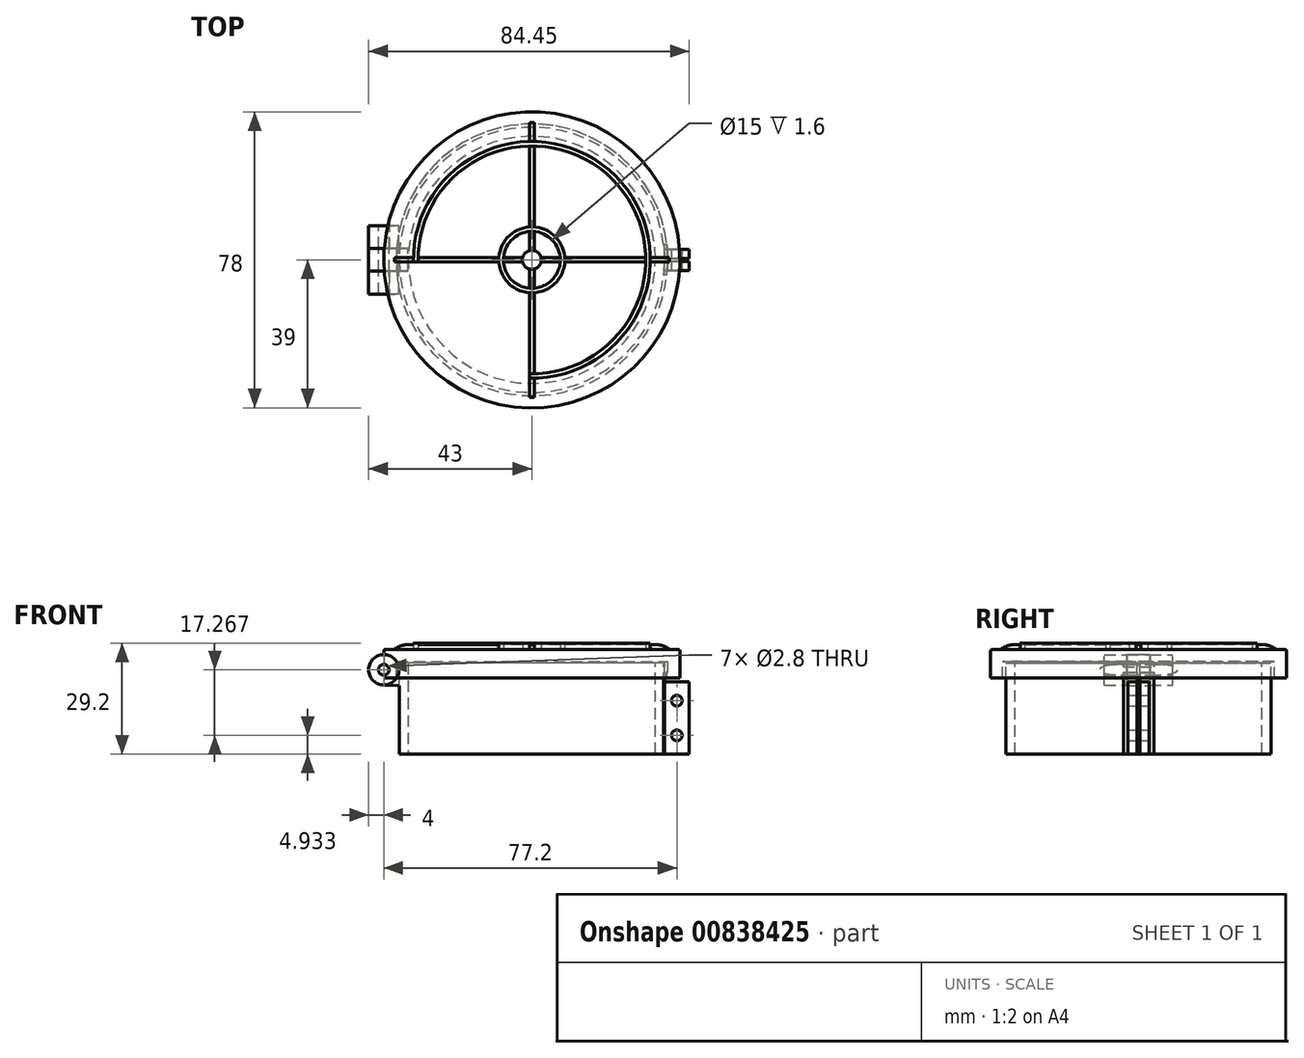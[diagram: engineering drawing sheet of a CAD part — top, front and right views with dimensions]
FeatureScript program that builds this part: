
annotation { "Feature Type Name" : "Feature", "Feature Type Description" : "" }
export const myFeature = defineFeature(function(context is Context, id is Id, definition is map)
    precondition{}
    {
        {
            var Q0;
            Q0=qCreatedBy(makeId("Front.planeOp"),FACE);
            var sketch = newSketch(context, id + "F0", { "sketchPlane" : qUnion([Q0])});
            skLineSegment(sketch, "E0", {"start": v(-39, 2) * mm, "end": v(-39, 9.6) * mm});
            skLineSegment(sketch, "E1", {"start": v(-39, 9.6) * mm, "end": v(0, 9.6) * mm});
            skLineSegment(sketch, "E2", {"start": v(0, 9.6) * mm, "end": v(0, 6.4) * mm});
            skLineSegment(sketch, "E3", {"start": v(0, 6.4) * mm, "end": v(-35.8, 6.4) * mm});
            skLineSegment(sketch, "E4", {"start": v(-35.8, 6.4) * mm, "end": v(-35.8, 2) * mm});
            skLineSegment(sketch, "E5", {"start": v(-35.8, 2) * mm, "end": v(-39, 2) * mm});
            skCircle(sketch, "E6", {"center": v(-39, 4.2) * mm, "radius": 4 * mm});
            skCircle(sketch, "E7", {"center": v(-39, 4.2) * mm, "radius": 1.4 * mm});
            skLineSegment(sketch, "E8.MirrorCS", {"start": v(39, 9.6) * mm, "end": v(0, 9.6) * mm});
            skLineSegment(sketch, "E9.MirrorCS", {"start": v(0, 6.4) * mm, "end": v(35.8, 6.4) * mm});
            skLineSegment(sketch, "E10.MirrorCS", {"start": v(35.8, 6.4) * mm, "end": v(35.8, 2) * mm});
            skLineSegment(sketch, "E11.MirrorCS", {"start": v(35.8, 2) * mm, "end": v(39, 2) * mm});
            skLineSegment(sketch, "E12.MirrorCS", {"start": v(39, 2) * mm, "end": v(39, 9.6) * mm});
            skCircle(sketch, "E13", {"center": v(35.8, 2.8) * mm, "radius": 0.8 * mm});
            skSolve(sketch);
        }
        {
            var Q0;
            Q0=qCreatedBy(makeId("Front.planeOp"),FACE);
            var sketch = newSketch(context, id + "F1", { "sketchPlane" : qUnion([Q0])});
            skLineSegment(sketch, "E14.bottom", {"start": v(-34.95, 6) * mm, "end": v(-32.55, 6) * mm});
            skLineSegment(sketch, "E14.top", {"start": v(-34.95, -18) * mm, "end": v(-32.55, -18) * mm});
            skLineSegment(sketch, "E14.left", {"start": v(-34.95, 6) * mm, "end": v(-34.95, -18) * mm});
            skLineSegment(sketch, "E14.right", {"start": v(-32.55, 6) * mm, "end": v(-32.55, -18) * mm});
            skCircle(sketch, "E15", {"center": v(-39, 4.2) * mm, "radius": 4 * mm});
            skCircle(sketch, "E16", {"center": v(-39, 4.2) * mm, "radius": 1.4 * mm});
            skLineSegment(sketch, "E17", {"start": v(-34.95, 0) * mm, "end": v(-39.2, 0.2) * mm});
            skLineSegment(sketch, "E18.MirrorCS", {"start": v(32.55, 6) * mm, "end": v(32.55, -18) * mm});
            skLineSegment(sketch, "E19.MirrorCS", {"start": v(34.95, 6) * mm, "end": v(34.95, -18) * mm});
            skLineSegment(sketch, "E20.MirrorCS", {"start": v(34.95, 6) * mm, "end": v(32.55, 6) * mm});
            skLineSegment(sketch, "E21.MirrorCS", {"start": v(34.95, -18) * mm, "end": v(32.55, -18) * mm});
            skCircle(sketch, "E22", {"center": v(34.95, 4.2) * mm, "radius": 0.8 * mm});
            skLineSegment(sketch, "E23", {"start": v(34.95, 1) * mm, "end": v(41.45, 1) * mm});
            skLineSegment(sketch, "E24", {"start": v(41.45, 1) * mm, "end": v(41.45, -18) * mm});
            skLineSegment(sketch, "E25", {"start": v(41.45, -18) * mm, "end": v(34.95, -18) * mm});
            skLineSegment(sketch, "E26", {"start": v(38.2, 1) * mm, "end": v(38.2, -18) * mm, "construction": true});
            skCircle(sketch, "E27", {"center": v(38.2, -3.93) * mm, "radius": 1.4 * mm});
            skCircle(sketch, "E28", {"center": v(38.2, -13.07) * mm, "radius": 1.4 * mm});
            skLineSegment(sketch, "E29", {"start": v(-34.95, 6) * mm, "end": v(-35.43, 6) * mm});
            skSolve(sketch);
        }
        {
            var Q0;
            {var subQ3=sQuery(id+"F1.wireOp",EDGE,"E14.bottom");Q0=makeQuery(id+"F1.imprint","IMPRINT",FACE,{"disambiguationData":[TD([[makeQuery(id+"F1.imprint","IMPRINT",EDGE,{"derivedFrom":subQ3}),-1.0]])]});}
            var Q1;
            Q1=sQuery(id+"F0.wireOp",EDGE,"E2");
            revolve(context, id + "F2", {"surfaceOperationType" : NewSurfaceOperationType.NEW, "entities" : qUnion([Q0]), "axis" : qUnion([Q1]), "revolveType" : RevolveType.FULL});
        }
        {
            var Q0;
            {var subQ0=sQuery(id+"F1.wireOp",EDGE,"E22");var subQ1=sQuery(id+"F1.wireOp",EDGE,"E19.MirrorCS");var subQ2=makeQuery(id+"F1.imprint","INTERSECT",VERTEX,{"disambiguationData":[OD(0.0)],"derivedFrom":[subQ1,subQ0]});Q0=makeQuery(id+"F1.imprint","IMPRINT",FACE,{"disambiguationData":[TD([[makeQuery(id+"F1.imprint","IMPRINT",EDGE,{"disambiguationData":[TD([[subQ2,-1.0]])],"derivedFrom":subQ1}),1.0]])]});}
            var Q1;
            {var subQ0=sQuery(id+"F1.wireOp",EDGE,"E22");var subQ1=sQuery(id+"F1.wireOp",EDGE,"E19.MirrorCS");var subQ2=makeQuery(id+"F1.imprint","INTERSECT",VERTEX,{"disambiguationData":[OD(0.0)],"derivedFrom":[subQ1,subQ0]});Q1=makeQuery(id+"F1.imprint","IMPRINT",FACE,{"disambiguationData":[TD([[makeQuery(id+"F1.imprint","IMPRINT",EDGE,{"disambiguationData":[TD([[subQ2,-1.0]])],"derivedFrom":subQ1}),-1.0]])]});}
            extrude(context, id + "F3", {"entities" : qUnion([Q0, Q1]), "operationType" : NewBodyOperationType.ADD, "endBound" : BoundingType.SYMMETRIC, "depth" : 8 * mm, "offsetDistance" : 25 * mm});
        }
        {
            var Q0;
            {var subQ1=sQuery(id+"F1.wireOp",EDGE,"E23");Q0=makeQuery(id+"F1.imprint","IMPRINT",FACE,{"disambiguationData":[TD([[makeQuery(id+"F1.imprint","IMPRINT",EDGE,{"derivedFrom":subQ1}),-1.0]])]});}
            var Q1;
            Q1=makeQuery(id+"F1.imprint","IMPRINT",FACE,{"disambiguationData":[TD([[makeQuery(id+"F1.imprint","IMPRINT",EDGE,{"derivedFrom":sQuery(id+"F1.wireOp",EDGE,"E18.MirrorCS")}),1.0]])]});
            extrude(context, id + "F4", {"entities" : qUnion([Q0, Q1]), "operationType" : NewBodyOperationType.ADD, "endBound" : BoundingType.SYMMETRIC, "depth" : 2.8 * 2 * mm, "offsetDistance" : 25 * mm});
        }
        {
            var Q0;
            Q0=qCreatedBy(makeId("Front.planeOp"),FACE);
            var sketch = newSketch(context, id + "F5", { "sketchPlane" : qUnion([Q0])});
            skLineSegment(sketch, "E30.bottom", {"start": v(30.27, 7.43) * mm, "end": v(42.44, 7.43) * mm});
            skLineSegment(sketch, "E30.top", {"start": v(30.27, -18.9) * mm, "end": v(42.44, -18.9) * mm});
            skLineSegment(sketch, "E30.left", {"start": v(30.27, 7.43) * mm, "end": v(30.27, -18.9) * mm});
            skLineSegment(sketch, "E30.right", {"start": v(42.44, 7.43) * mm, "end": v(42.44, -18.9) * mm});
            skSolve(sketch);
        }
        {
            var Q0;
            Q0=makeQuery(id+"F5.imprint","IMPRINT",FACE,{"disambiguationData":[TD([[makeQuery(id+"F5.imprint","IMPRINT",EDGE,{"derivedFrom":sQuery(id+"F5.wireOp",EDGE,"E30.bottom")}),-1.0]])]});
            extrude(context, id + "F6", {"entities" : qUnion([Q0]), "operationType" : NewBodyOperationType.REMOVE, "endBound" : BoundingType.SYMMETRIC, "depth" : 0.8 * mm, "offsetDistance" : 25 * mm});
        }
        {
            var Q0;
            Q0=makeQuery(id+"F1.imprint","IMPRINT",FACE,{"disambiguationData":[TD([[makeQuery(id+"F1.imprint","IMPRINT",EDGE,{"derivedFrom":sQuery(id+"F1.wireOp",EDGE,"E15")}),1.0]])]});
            var Q1;
            {var subQ2=sQuery(id+"F1.wireOp",EDGE,"E17");Q1=makeQuery(id+"F1.imprint","IMPRINT",FACE,{"disambiguationData":[TD([[makeQuery(id+"F1.imprint","IMPRINT",EDGE,{"derivedFrom":subQ2}),-1.0]])]});}
            var Q2;
            {var subQ3=sQuery(id+"F1.wireOp",EDGE,"E14.bottom");Q2=makeQuery(id+"F1.imprint","IMPRINT",FACE,{"disambiguationData":[TD([[makeQuery(id+"F1.imprint","IMPRINT",EDGE,{"derivedFrom":subQ3}),-1.0]])]});}
            extrude(context, id + "F7", {"entities" : qUnion([Q0, Q1, Q2]), "endBound" : BoundingType.SYMMETRIC, "depth" : 18 / 3 * mm, "offsetDistance" : 25 * mm});
        }
        {
            var Q0;
            {var subQ4=sQuery(id+"F0.wireOp",EDGE,"E1");Q0=makeQuery(id+"F0.imprint","IMPRINT",FACE,{"disambiguationData":[TD([[makeQuery(id+"F0.imprint","IMPRINT",EDGE,{"derivedFrom":subQ4}),-1.0]])]});}
            var Q1;
            {var subQ0=sQuery(id+"F0.wireOp",EDGE,"E4");Q1=makeQuery(id+"F0.imprint","IMPRINT",FACE,{"disambiguationData":[TD([[makeQuery(id+"F0.imprint","IMPRINT",EDGE,{"derivedFrom":subQ0}),-1.0]])]});}
            var Q2;
            {var subQ0=sQuery(id+"F0.wireOp",EDGE,"E7");var subQ1=sQuery(id+"F0.wireOp",EDGE,"E0");var subQ2=makeQuery(id+"F0.imprint","INTERSECT",VERTEX,{"disambiguationData":[OD(0.0)],"derivedFrom":[subQ1,subQ0]});Q2=makeQuery(id+"F0.imprint","IMPRINT",FACE,{"disambiguationData":[TD([[makeQuery(id+"F0.imprint","IMPRINT",EDGE,{"disambiguationData":[TD([[subQ2,-1.0]])],"derivedFrom":subQ1}),-1.0]])]});}
            var Q3;
            Q3=sQuery(id+"F0.wireOp",EDGE,"E2");
            revolve(context, id + "F8", {"surfaceOperationType" : NewSurfaceOperationType.NEW, "entities" : qUnion([Q0, Q1, Q2]), "axis" : qUnion([Q3]), "revolveType" : RevolveType.FULL});
        }
        {
            var Q0;
            {var subQ0=sQuery(id+"F0.wireOp",EDGE,"E4");Q0=makeQuery(id+"F0.imprint","IMPRINT",FACE,{"disambiguationData":[TD([[makeQuery(id+"F0.imprint","IMPRINT",EDGE,{"derivedFrom":subQ0}),1.0]])]});}
            var Q1;
            {var subQ0=sQuery(id+"F0.wireOp",EDGE,"E4");Q1=makeQuery(id+"F0.imprint","IMPRINT",FACE,{"disambiguationData":[TD([[makeQuery(id+"F0.imprint","IMPRINT",EDGE,{"derivedFrom":subQ0}),-1.0]])]});}
            var Q2;
            Q2=sQuery(id+"F0.wireOp",EDGE,"E6");
            var Q3;
            Q3=sQuery(id+"F0.wireOp",EDGE,"E7");
            extrude(context, id + "F9", {"entities" : qUnion([Q0, Q1]), "surfaceEntities" : qUnion([Q2, Q3]), "endBound" : BoundingType.SYMMETRIC, "depth" : 18 * mm, "offsetDistance" : 25 * mm});
        }
        {
            var Q0;
            {var subQ0=sQuery(id+"F0.wireOp",EDGE,"E4");Q0=makeQuery(id+"F0.imprint","IMPRINT",FACE,{"disambiguationData":[TD([[makeQuery(id+"F0.imprint","IMPRINT",EDGE,{"derivedFrom":subQ0}),1.0]])]});}
            var Q1;
            {var subQ0=sQuery(id+"F0.wireOp",EDGE,"E4");Q1=makeQuery(id+"F0.imprint","IMPRINT",FACE,{"disambiguationData":[TD([[makeQuery(id+"F0.imprint","IMPRINT",EDGE,{"derivedFrom":subQ0}),-1.0]])]});}
            extrude(context, id + "F10", {"entities" : qUnion([Q0, Q1]), "endBound" : BoundingType.SYMMETRIC, "oppositeDirection" : true, "depth" : 6 * mm, "offsetDistance" : 25 * mm});
        }
        {
            var Q0;
            Q0=makeQuery(id+"F10.opExtrude","SWEPT_BODY",BODY,{"disambiguationData":[OSD([sQuery(id+"F0.wireOp",EDGE,"E6"),sQuery(id+"F0.wireOp",EDGE,"E7")])]});
            var Q1;
            Q1=makeQuery(id+"F9.opExtrude","SWEPT_BODY",BODY,{"disambiguationData":[OSD([sQuery(id+"F0.wireOp",EDGE,"E6"),sQuery(id+"F0.wireOp",EDGE,"E7")])]});
            var Q2;
            Q2=makeQuery(id+"F8.opRevolve","SWEPT_BODY",BODY,{"disambiguationData":[OSD([sQuery(id+"F0.wireOp",EDGE,"E0"),sQuery(id+"F0.wireOp",EDGE,"E1"),sQuery(id+"F0.wireOp",EDGE,"E2"),sQuery(id+"F0.wireOp",EDGE,"E3"),sQuery(id+"F0.wireOp",EDGE,"E4"),sQuery(id+"F0.wireOp",EDGE,"E5")])]});
            booleanBodies(context, id + "F11", {"operationType" : BooleanOperationType.SUBTRACTION, "tools" : qUnion([Q0]), "targets" : qUnion([Q1, Q2])});
        }
        {
            var Q0;
            {var subQ0=sQuery(id+"F0.wireOp",EDGE,"E7");var subQ1=sQuery(id+"F0.wireOp",EDGE,"E0");var subQ2=makeQuery(id+"F0.imprint","INTERSECT",VERTEX,{"disambiguationData":[OD(0.0)],"derivedFrom":[subQ1,subQ0]});Q0=makeQuery(id+"F0.imprint","IMPRINT",FACE,{"disambiguationData":[TD([[makeQuery(id+"F0.imprint","IMPRINT",EDGE,{"disambiguationData":[TD([[subQ2,-1.0]])],"derivedFrom":subQ1}),1.0]])]});}
            var Q1;
            Q1=makeQuery(id+"F1.imprint","IMPRINT",FACE,{"disambiguationData":[TD([[makeQuery(id+"F1.imprint","IMPRINT",EDGE,{"derivedFrom":sQuery(id+"F1.wireOp",EDGE,"E16")}),1.0]])]});
            extrude(context, id + "F12", {"entities" : qUnion([Q0, Q1]), "endBound" : BoundingType.SYMMETRIC, "oppositeDirection" : true, "depth" : 25 * mm, "offsetDistance" : 25 * mm});
        }
        {
            var Q0;
            Q0=makeQuery(id+"F12.opExtrude","SWEPT_BODY",BODY,{"disambiguationData":[OSD([sQuery(id+"F1.wireOp",EDGE,"E16")])]});
            var Q1;
            Q1=makeQuery(id+"F12.opExtrude","SWEPT_BODY",BODY,{"disambiguationData":[OSD([sQuery(id+"F0.wireOp",EDGE,"E0"),sQuery(id+"F0.wireOp",EDGE,"E7")])]});
            var Q2;
            Q2=makeQuery(id+"F8.opRevolve","SWEPT_BODY",BODY,{"disambiguationData":[OSD([sQuery(id+"F0.wireOp",EDGE,"E0"),sQuery(id+"F0.wireOp",EDGE,"E1"),sQuery(id+"F0.wireOp",EDGE,"E2"),sQuery(id+"F0.wireOp",EDGE,"E3"),sQuery(id+"F0.wireOp",EDGE,"E4"),sQuery(id+"F0.wireOp",EDGE,"E5")])]});
            var Q3;
            Q3=makeQuery(id+"F11.opBoolean","SPLIT",BODY,{"disambiguationData":[OD(0.0)],"derivedFrom":makeQuery(id+"F9.opExtrude","SWEPT_BODY",BODY,{"disambiguationData":[OSD([sQuery(id+"F0.wireOp",EDGE,"E6"),sQuery(id+"F0.wireOp",EDGE,"E7")])]})});
            var Q4;
            Q4=makeQuery(id+"F11.opBoolean","SPLIT",BODY,{"disambiguationData":[OD(1.0)],"derivedFrom":makeQuery(id+"F9.opExtrude","SWEPT_BODY",BODY,{"disambiguationData":[OSD([sQuery(id+"F0.wireOp",EDGE,"E6"),sQuery(id+"F0.wireOp",EDGE,"E7")])]})});
            booleanBodies(context, id + "F13", {"operationType" : BooleanOperationType.SUBTRACTION, "tools" : qUnion([Q0, Q1]), "targets" : qUnion([Q2, Q3, Q4])});
        }
        {
            var Q0;
            {var subQ0=sQuery(id+"F0.wireOp",EDGE,"E13");var subQ1=sQuery(id+"F0.wireOp",EDGE,"E10.MirrorCS");var subQ3=makeQuery(id+"F0.imprint","INTERSECT",VERTEX,{"derivedFrom":[subQ1,subQ0]});Q0=makeQuery(id+"F0.imprint","IMPRINT",FACE,{"disambiguationData":[TD([[makeQuery(id+"F0.imprint","IMPRINT",EDGE,{"disambiguationData":[TD([[subQ3,-1.0]])],"derivedFrom":subQ1}),-1.0]])]});}
            extrude(context, id + "F14", {"entities" : qUnion([Q0]), "operationType" : NewBodyOperationType.ADD, "endBound" : BoundingType.SYMMETRIC, "depth" : 8 * mm, "offsetDistance" : 25 * mm});
        }
        {
            var Q0;
            Q0=makeQuery(id+"F8.opRevolve","SWEPT_FACE",FACE,{"disambiguationData":[OSD([sQuery(id+"F0.wireOp",EDGE,"E1")])]});
            var sketch = newSketch(context, id + "F15", { "sketchPlane" : qUnion([Q0])});
            skCircle(sketch, "E31", {"center": v(0, 0) * mm, "radius": 7.5 * mm});
            skCircle(sketch, "E32", {"center": v(0, 0) * mm, "radius": 30 * mm});
            skCircle(sketch, "E33.0", {"center": v(0, 0) * mm, "radius": 31.2 * mm});
            skLineSegment(sketch, "E34", {"start": v(36.2, -0.6) * mm, "end": v(-36.2, -0.6) * mm});
            skLineSegment(sketch, "E35", {"start": v(-36.2, -0.6) * mm, "end": v(-36.2, 0) * mm});
            skLineSegment(sketch, "E36", {"start": v(-36.2, 0) * mm, "end": v(36.2, 0) * mm, "construction": true});
            skLineSegment(sketch, "E37", {"start": v(36.2, 0) * mm, "end": v(36.2, -0.6) * mm});
            skLineSegment(sketch, "E38.MirrorCS", {"start": v(36.2, 0.6) * mm, "end": v(-36.2, 0.6) * mm});
            skLineSegment(sketch, "E39.MirrorCS", {"start": v(36.2, 0) * mm, "end": v(36.2, 0.6) * mm});
            skLineSegment(sketch, "E40.MirrorCS", {"start": v(-36.2, 0.6) * mm, "end": v(-36.2, 0) * mm});
            skLineSegment(sketch, "E41", {"start": v(0, 0) * mm, "end": v(0, -36.2) * mm, "construction": true});
            skLineSegment(sketch, "E42", {"start": v(0, -36.2) * mm, "end": v(-0.6, -36.2) * mm});
            skLineSegment(sketch, "E43", {"start": v(-0.6, -36.2) * mm, "end": v(-0.6, -0.6) * mm});
            skLineSegment(sketch, "E44.MirrorCS", {"start": v(0, -36.2) * mm, "end": v(0.6, -36.2) * mm});
            skLineSegment(sketch, "E45.MirrorCS", {"start": v(0.6, -36.2) * mm, "end": v(0.6, -0.6) * mm});
            skLineSegment(sketch, "E46.MirrorCS", {"start": v(0.6, 36.2) * mm, "end": v(0.6, 0.6) * mm});
            skLineSegment(sketch, "E47.MirrorCS", {"start": v(-0.6, 36.2) * mm, "end": v(-0.6, 0.6) * mm});
            skLineSegment(sketch, "E48.MirrorCS", {"start": v(0, 36.2) * mm, "end": v(0.6, 36.2) * mm});
            skLineSegment(sketch, "E49.MirrorCS", {"start": v(0, 36.2) * mm, "end": v(-0.6, 36.2) * mm});
            skCircle(sketch, "E50.0", {"center": v(0, 0) * mm, "radius": 8.7 * mm});
            skCircle(sketch, "E51", {"center": v(0, 0) * mm, "radius": 2.5 * mm});
            skSolve(sketch);
        }
        {
            var Q0;
            {var subQ0=sQuery(id+"F15.wireOp",EDGE,"E43");var subQ1=sQuery(id+"F15.wireOp",EDGE,"E34");var subQ2=makeQuery(id+"F15.imprint","INTERSECT",VERTEX,{"derivedFrom":[subQ1,subQ0]});Q0=makeQuery(id+"F15.imprint","IMPRINT",FACE,{"disambiguationData":[TD([[makeQuery(id+"F15.imprint","IMPRINT",EDGE,{"disambiguationData":[TD([[subQ2,-1.0]])],"derivedFrom":subQ1}),1.0]])]});}
            var Q1;
            {var subQ0=sQuery(id+"F15.wireOp",EDGE,"E43");var subQ1=sQuery(id+"F15.wireOp",EDGE,"E34");var subQ2=makeQuery(id+"F15.imprint","INTERSECT",VERTEX,{"derivedFrom":[subQ1,subQ0]});Q1=makeQuery(id+"F15.imprint","IMPRINT",FACE,{"disambiguationData":[TD([[makeQuery(id+"F15.imprint","IMPRINT",EDGE,{"disambiguationData":[TD([[subQ2,1.0]])],"derivedFrom":subQ1}),1.0]])]});}
            var Q2;
            {var subQ0=sQuery(id+"F15.wireOp",EDGE,"E45.MirrorCS");var subQ1=sQuery(id+"F15.wireOp",EDGE,"E34");var subQ2=makeQuery(id+"F15.imprint","INTERSECT",VERTEX,{"derivedFrom":[subQ1,subQ0]});Q2=makeQuery(id+"F15.imprint","IMPRINT",FACE,{"disambiguationData":[TD([[makeQuery(id+"F15.imprint","IMPRINT",EDGE,{"disambiguationData":[TD([[subQ2,1.0]])],"derivedFrom":subQ1}),1.0]])]});}
            var Q3;
            {var subQ0=sQuery(id+"F15.wireOp",EDGE,"E34");var subQ7=makeQuery(id+"F15.imprint","INTERSECT",VERTEX,{"derivedFrom":[subQ0,sQuery(id+"F15.wireOp",EDGE,"E45.MirrorCS")]});Q3=makeQuery(id+"F15.imprint","IMPRINT",FACE,{"disambiguationData":[TD([[makeQuery(id+"F15.imprint","IMPRINT",EDGE,{"disambiguationData":[TD([[subQ7,1.0]])],"derivedFrom":subQ0}),-1.0]])]});}
            var Q4;
            {var subQ0=sQuery(id+"F15.wireOp",EDGE,"E47.MirrorCS");var subQ1=sQuery(id+"F15.wireOp",EDGE,"E38.MirrorCS");var subQ2=makeQuery(id+"F15.imprint","INTERSECT",VERTEX,{"derivedFrom":[subQ1,subQ0]});Q4=makeQuery(id+"F15.imprint","IMPRINT",FACE,{"disambiguationData":[TD([[makeQuery(id+"F15.imprint","IMPRINT",EDGE,{"disambiguationData":[TD([[subQ2,-1.0]])],"derivedFrom":subQ1}),-1.0]])]});}
            var Q5;
            {var subQ0=sQuery(id+"F15.wireOp",EDGE,"E46.MirrorCS");var subQ1=sQuery(id+"F15.wireOp",EDGE,"E38.MirrorCS");var subQ2=makeQuery(id+"F15.imprint","INTERSECT",VERTEX,{"derivedFrom":[subQ1,subQ0]});Q5=makeQuery(id+"F15.imprint","IMPRINT",FACE,{"disambiguationData":[TD([[makeQuery(id+"F15.imprint","IMPRINT",EDGE,{"disambiguationData":[TD([[subQ2,-1.0]])],"derivedFrom":subQ1}),-1.0]])]});}
            var Q6;
            {var subQ0=sQuery(id+"F15.wireOp",EDGE,"E46.MirrorCS");var subQ1=sQuery(id+"F15.wireOp",EDGE,"E38.MirrorCS");var subQ2=makeQuery(id+"F15.imprint","INTERSECT",VERTEX,{"derivedFrom":[subQ1,subQ0]});Q6=makeQuery(id+"F15.imprint","IMPRINT",FACE,{"disambiguationData":[TD([[makeQuery(id+"F15.imprint","IMPRINT",EDGE,{"disambiguationData":[TD([[subQ2,1.0]])],"derivedFrom":subQ1}),-1.0]])]});}
            var Q7;
            {var subQ0=sQuery(id+"F15.wireOp",EDGE,"E45.MirrorCS");var subQ1=sQuery(id+"F15.wireOp",EDGE,"E31");var subQ2=makeQuery(id+"F15.imprint","INTERSECT",VERTEX,{"derivedFrom":[subQ1,subQ0]});Q7=makeQuery(id+"F15.imprint","IMPRINT",FACE,{"disambiguationData":[TD([[makeQuery(id+"F15.imprint","IMPRINT",EDGE,{"disambiguationData":[TD([[subQ2,-1.0]])],"derivedFrom":subQ1}),-1.0]])]});}
            var Q8;
            {var subQ0=sQuery(id+"F15.wireOp",EDGE,"E46.MirrorCS");var subQ1=sQuery(id+"F15.wireOp",EDGE,"E31");var subQ2=makeQuery(id+"F15.imprint","INTERSECT",VERTEX,{"derivedFrom":[subQ1,subQ0]});Q8=makeQuery(id+"F15.imprint","IMPRINT",FACE,{"disambiguationData":[TD([[makeQuery(id+"F15.imprint","IMPRINT",EDGE,{"disambiguationData":[TD([[subQ2,1.0]])],"derivedFrom":subQ1}),-1.0]])]});}
            var Q9;
            {var subQ0=sQuery(id+"F15.wireOp",EDGE,"E47.MirrorCS");var subQ1=sQuery(id+"F15.wireOp",EDGE,"E31");var subQ2=makeQuery(id+"F15.imprint","INTERSECT",VERTEX,{"derivedFrom":[subQ1,subQ0]});Q9=makeQuery(id+"F15.imprint","IMPRINT",FACE,{"disambiguationData":[TD([[makeQuery(id+"F15.imprint","IMPRINT",EDGE,{"disambiguationData":[TD([[subQ2,-1.0]])],"derivedFrom":subQ1}),-1.0]])]});}
            var Q10;
            {var subQ0=sQuery(id+"F15.wireOp",EDGE,"E34");var subQ1=sQuery(id+"F15.wireOp",EDGE,"E31");var subQ2=makeQuery(id+"F15.imprint","INTERSECT",VERTEX,{"disambiguationData":[OD(0.0)],"derivedFrom":[subQ1,subQ0]});Q10=makeQuery(id+"F15.imprint","IMPRINT",FACE,{"disambiguationData":[TD([[makeQuery(id+"F15.imprint","IMPRINT",EDGE,{"disambiguationData":[TD([[subQ2,-1.0]])],"derivedFrom":subQ1}),-1.0]])]});}
            var Q11;
            {var subQ0=sQuery(id+"F15.wireOp",EDGE,"E46.MirrorCS");var subQ1=sQuery(id+"F15.wireOp",EDGE,"E31");var subQ2=makeQuery(id+"F15.imprint","INTERSECT",VERTEX,{"derivedFrom":[subQ1,subQ0]});Q11=makeQuery(id+"F15.imprint","IMPRINT",FACE,{"disambiguationData":[TD([[makeQuery(id+"F15.imprint","IMPRINT",EDGE,{"disambiguationData":[TD([[subQ2,-1.0]])],"derivedFrom":subQ1}),-1.0]])]});}
            var Q12;
            {var subQ0=sQuery(id+"F15.wireOp",EDGE,"E38.MirrorCS");var subQ1=sQuery(id+"F15.wireOp",EDGE,"E31");var subQ2=makeQuery(id+"F15.imprint","INTERSECT",VERTEX,{"disambiguationData":[OD(0.0)],"derivedFrom":[subQ1,subQ0]});Q12=makeQuery(id+"F15.imprint","IMPRINT",FACE,{"disambiguationData":[TD([[makeQuery(id+"F15.imprint","IMPRINT",EDGE,{"disambiguationData":[TD([[subQ2,1.0]])],"derivedFrom":subQ1}),-1.0]])]});}
            var Q13;
            {var subQ0=sQuery(id+"F15.wireOp",EDGE,"E43");var subQ1=sQuery(id+"F15.wireOp",EDGE,"E31");var subQ2=makeQuery(id+"F15.imprint","INTERSECT",VERTEX,{"derivedFrom":[subQ1,subQ0]});Q13=makeQuery(id+"F15.imprint","IMPRINT",FACE,{"disambiguationData":[TD([[makeQuery(id+"F15.imprint","IMPRINT",EDGE,{"disambiguationData":[TD([[subQ2,-1.0]])],"derivedFrom":subQ1}),-1.0]])]});}
            var Q14;
            {var subQ0=sQuery(id+"F15.wireOp",EDGE,"E38.MirrorCS");var subQ1=sQuery(id+"F15.wireOp",EDGE,"E31");var subQ2=makeQuery(id+"F15.imprint","INTERSECT",VERTEX,{"disambiguationData":[OD(1.0)],"derivedFrom":[subQ1,subQ0]});Q14=makeQuery(id+"F15.imprint","IMPRINT",FACE,{"disambiguationData":[TD([[makeQuery(id+"F15.imprint","IMPRINT",EDGE,{"disambiguationData":[TD([[subQ2,-1.0]])],"derivedFrom":subQ1}),-1.0]])]});}
            var Q15;
            {var subQ0=sQuery(id+"F15.wireOp",EDGE,"E43");var subQ1=sQuery(id+"F15.wireOp",EDGE,"E32");var subQ2=makeQuery(id+"F15.imprint","INTERSECT",VERTEX,{"derivedFrom":[subQ1,subQ0]});Q15=makeQuery(id+"F15.imprint","IMPRINT",FACE,{"disambiguationData":[TD([[makeQuery(id+"F15.imprint","IMPRINT",EDGE,{"disambiguationData":[TD([[subQ2,-1.0]])],"derivedFrom":subQ1}),-1.0]])]});}
            var Q16;
            {var subQ0=sQuery(id+"F15.wireOp",EDGE,"E38.MirrorCS");var subQ1=sQuery(id+"F15.wireOp",EDGE,"E32");var subQ2=makeQuery(id+"F15.imprint","INTERSECT",VERTEX,{"disambiguationData":[OD(0.0)],"derivedFrom":[subQ1,subQ0]});Q16=makeQuery(id+"F15.imprint","IMPRINT",FACE,{"disambiguationData":[TD([[makeQuery(id+"F15.imprint","IMPRINT",EDGE,{"disambiguationData":[TD([[subQ2,1.0]])],"derivedFrom":subQ1}),-1.0]])]});}
            var Q17;
            {var subQ0=sQuery(id+"F15.wireOp",EDGE,"E46.MirrorCS");var subQ1=sQuery(id+"F15.wireOp",EDGE,"E32");var subQ2=makeQuery(id+"F15.imprint","INTERSECT",VERTEX,{"derivedFrom":[subQ1,subQ0]});Q17=makeQuery(id+"F15.imprint","IMPRINT",FACE,{"disambiguationData":[TD([[makeQuery(id+"F15.imprint","IMPRINT",EDGE,{"disambiguationData":[TD([[subQ2,-1.0]])],"derivedFrom":subQ1}),-1.0]])]});}
            var Q18;
            {var subQ0=sQuery(id+"F15.wireOp",EDGE,"E38.MirrorCS");var subQ1=sQuery(id+"F15.wireOp",EDGE,"E32");var subQ2=makeQuery(id+"F15.imprint","INTERSECT",VERTEX,{"disambiguationData":[OD(1.0)],"derivedFrom":[subQ1,subQ0]});Q18=makeQuery(id+"F15.imprint","IMPRINT",FACE,{"disambiguationData":[TD([[makeQuery(id+"F15.imprint","IMPRINT",EDGE,{"disambiguationData":[TD([[subQ2,-1.0]])],"derivedFrom":subQ1}),-1.0]])]});}
            var Q19;
            {var subQ0=sQuery(id+"F15.wireOp",EDGE,"E34");var subQ1=sQuery(id+"F15.wireOp",EDGE,"E32");var subQ2=makeQuery(id+"F15.imprint","INTERSECT",VERTEX,{"disambiguationData":[OD(0.0)],"derivedFrom":[subQ1,subQ0]});Q19=makeQuery(id+"F15.imprint","IMPRINT",FACE,{"disambiguationData":[TD([[makeQuery(id+"F15.imprint","IMPRINT",EDGE,{"disambiguationData":[TD([[subQ2,-1.0]])],"derivedFrom":subQ1}),-1.0]])]});}
            var Q20;
            {var subQ0=sQuery(id+"F15.wireOp",EDGE,"E45.MirrorCS");var subQ1=sQuery(id+"F15.wireOp",EDGE,"E32");var subQ2=makeQuery(id+"F15.imprint","INTERSECT",VERTEX,{"derivedFrom":[subQ1,subQ0]});Q20=makeQuery(id+"F15.imprint","IMPRINT",FACE,{"disambiguationData":[TD([[makeQuery(id+"F15.imprint","IMPRINT",EDGE,{"disambiguationData":[TD([[subQ2,-1.0]])],"derivedFrom":subQ1}),-1.0]])]});}
            var Q21;
            {var subQ0=sQuery(id+"F15.wireOp",EDGE,"E46.MirrorCS");var subQ1=sQuery(id+"F15.wireOp",EDGE,"E32");var subQ2=makeQuery(id+"F15.imprint","INTERSECT",VERTEX,{"derivedFrom":[subQ1,subQ0]});Q21=makeQuery(id+"F15.imprint","IMPRINT",FACE,{"disambiguationData":[TD([[makeQuery(id+"F15.imprint","IMPRINT",EDGE,{"disambiguationData":[TD([[subQ2,1.0]])],"derivedFrom":subQ1}),-1.0]])]});}
            var Q22;
            {var subQ0=sQuery(id+"F15.wireOp",EDGE,"E47.MirrorCS");var subQ1=sQuery(id+"F15.wireOp",EDGE,"E32");var subQ2=makeQuery(id+"F15.imprint","INTERSECT",VERTEX,{"derivedFrom":[subQ1,subQ0]});Q22=makeQuery(id+"F15.imprint","IMPRINT",FACE,{"disambiguationData":[TD([[makeQuery(id+"F15.imprint","IMPRINT",EDGE,{"disambiguationData":[TD([[subQ2,-1.0]])],"derivedFrom":subQ1}),-1.0]])]});}
            extrude(context, id + "F16", {"entities" : qUnion([Q0, Q1, Q2, Q3, Q4, Q5, Q6, Q7, Q8, Q9, Q10, Q11, Q12, Q13, Q14, Q15, Q16, Q17, Q18, Q19, Q20, Q21, Q22]), "operationType" : NewBodyOperationType.ADD, "depth" : 1.6 * mm, "offsetDistance" : 25 * mm});
        }
        {
            var Q0;
            {var subQ4=sQuery(id+"F15.wireOp",EDGE,"E37");Q0=makeQuery(id+"F15.imprint","IMPRINT",FACE,{"disambiguationData":[TD([[makeQuery(id+"F15.imprint","IMPRINT",EDGE,{"derivedFrom":subQ4}),-1.0]])]});}
            var Q1;
            {var subQ0=sQuery(id+"F15.wireOp",EDGE,"E38.MirrorCS");var subQ1=sQuery(id+"F15.wireOp",EDGE,"E32");var subQ2=makeQuery(id+"F15.imprint","INTERSECT",VERTEX,{"disambiguationData":[OD(0.0)],"derivedFrom":[subQ1,subQ0]});Q1=makeQuery(id+"F15.imprint","IMPRINT",FACE,{"disambiguationData":[TD([[makeQuery(id+"F15.imprint","IMPRINT",EDGE,{"disambiguationData":[TD([[subQ2,1.0]])],"derivedFrom":subQ1}),1.0]])]});}
            var Q2;
            {var subQ1=sQuery(id+"F15.wireOp",EDGE,"E42");Q2=makeQuery(id+"F15.imprint","IMPRINT",FACE,{"disambiguationData":[TD([[makeQuery(id+"F15.imprint","IMPRINT",EDGE,{"derivedFrom":subQ1}),-1.0]])]});}
            var Q3;
            {var subQ0=sQuery(id+"F15.wireOp",EDGE,"E43");var subQ1=sQuery(id+"F15.wireOp",EDGE,"E32");var subQ2=makeQuery(id+"F15.imprint","INTERSECT",VERTEX,{"derivedFrom":[subQ1,subQ0]});Q3=makeQuery(id+"F15.imprint","IMPRINT",FACE,{"disambiguationData":[TD([[makeQuery(id+"F15.imprint","IMPRINT",EDGE,{"disambiguationData":[TD([[subQ2,-1.0]])],"derivedFrom":subQ1}),1.0]])]});}
            var Q4;
            {var subQ0=sQuery(id+"F15.wireOp",EDGE,"E35");Q4=makeQuery(id+"F15.imprint","IMPRINT",FACE,{"disambiguationData":[TD([[makeQuery(id+"F15.imprint","IMPRINT",EDGE,{"derivedFrom":subQ0}),-1.0]])]});}
            var Q5;
            {var subQ0=sQuery(id+"F15.wireOp",EDGE,"E38.MirrorCS");var subQ1=sQuery(id+"F15.wireOp",EDGE,"E32");var subQ2=makeQuery(id+"F15.imprint","INTERSECT",VERTEX,{"disambiguationData":[OD(1.0)],"derivedFrom":[subQ1,subQ0]});Q5=makeQuery(id+"F15.imprint","IMPRINT",FACE,{"disambiguationData":[TD([[makeQuery(id+"F15.imprint","IMPRINT",EDGE,{"disambiguationData":[TD([[subQ2,-1.0]])],"derivedFrom":subQ1}),1.0]])]});}
            var Q6;
            {var subQ0=sQuery(id+"F15.wireOp",EDGE,"E48.MirrorCS");Q6=makeQuery(id+"F15.imprint","IMPRINT",FACE,{"disambiguationData":[TD([[makeQuery(id+"F15.imprint","IMPRINT",EDGE,{"derivedFrom":subQ0}),-1.0]])]});}
            var Q7;
            {var subQ0=sQuery(id+"F15.wireOp",EDGE,"E46.MirrorCS");var subQ1=sQuery(id+"F15.wireOp",EDGE,"E32");var subQ2=makeQuery(id+"F15.imprint","INTERSECT",VERTEX,{"derivedFrom":[subQ1,subQ0]});Q7=makeQuery(id+"F15.imprint","IMPRINT",FACE,{"disambiguationData":[TD([[makeQuery(id+"F15.imprint","IMPRINT",EDGE,{"disambiguationData":[TD([[subQ2,-1.0]])],"derivedFrom":subQ1}),1.0]])]});}
            var Q8;
            {var subQ0=sQuery(id+"F15.wireOp",EDGE,"E38.MirrorCS");var subQ1=sQuery(id+"F15.wireOp",EDGE,"E31");var subQ2=makeQuery(id+"F15.imprint","INTERSECT",VERTEX,{"disambiguationData":[OD(0.0)],"derivedFrom":[subQ1,subQ0]});Q8=makeQuery(id+"F15.imprint","IMPRINT",FACE,{"disambiguationData":[TD([[makeQuery(id+"F15.imprint","IMPRINT",EDGE,{"disambiguationData":[TD([[subQ2,1.0]])],"derivedFrom":subQ1}),1.0]])]});}
            var Q9;
            {var subQ0=sQuery(id+"F15.wireOp",EDGE,"E43");var subQ1=sQuery(id+"F15.wireOp",EDGE,"E31");var subQ2=makeQuery(id+"F15.imprint","INTERSECT",VERTEX,{"derivedFrom":[subQ1,subQ0]});Q9=makeQuery(id+"F15.imprint","IMPRINT",FACE,{"disambiguationData":[TD([[makeQuery(id+"F15.imprint","IMPRINT",EDGE,{"disambiguationData":[TD([[subQ2,-1.0]])],"derivedFrom":subQ1}),1.0]])]});}
            var Q10;
            {var subQ0=sQuery(id+"F15.wireOp",EDGE,"E38.MirrorCS");var subQ1=sQuery(id+"F15.wireOp",EDGE,"E31");var subQ2=makeQuery(id+"F15.imprint","INTERSECT",VERTEX,{"disambiguationData":[OD(1.0)],"derivedFrom":[subQ1,subQ0]});Q10=makeQuery(id+"F15.imprint","IMPRINT",FACE,{"disambiguationData":[TD([[makeQuery(id+"F15.imprint","IMPRINT",EDGE,{"disambiguationData":[TD([[subQ2,-1.0]])],"derivedFrom":subQ1}),1.0]])]});}
            var Q11;
            {var subQ0=sQuery(id+"F15.wireOp",EDGE,"E46.MirrorCS");var subQ1=sQuery(id+"F15.wireOp",EDGE,"E31");var subQ2=makeQuery(id+"F15.imprint","INTERSECT",VERTEX,{"derivedFrom":[subQ1,subQ0]});Q11=makeQuery(id+"F15.imprint","IMPRINT",FACE,{"disambiguationData":[TD([[makeQuery(id+"F15.imprint","IMPRINT",EDGE,{"disambiguationData":[TD([[subQ2,-1.0]])],"derivedFrom":subQ1}),1.0]])]});}
            extrude(context, id + "F17", {"entities" : qUnion([Q0, Q1, Q2, Q3, Q4, Q5, Q6, Q7, Q8, Q9, Q10, Q11]), "operationType" : NewBodyOperationType.ADD, "depth" : 1.2 * mm, "offsetDistance" : 25 * mm});
        }
        {
            var Q0;
            {var subQ0=sQuery(id+"F15.wireOp",EDGE,"E33.0");var subQ1=sQuery(id+"F15.wireOp",EDGE,"E38.MirrorCS");Q0=makeQuery(id+"F17.boolean.opBoolean","SPLIT",EDGE,{"disambiguationData":[TD([makeQuery(id+"F17.opExtrude","SWEPT_FACE",FACE,{"disambiguationData":[OSD([subQ1]),TDD([makeQuery(id+"F15.imprint","IMPRINT",EDGE,{"disambiguationData":[TD([[makeQuery(id+"F15.imprint","INTERSECT",VERTEX,{"derivedFrom":[subQ1,sQuery(id+"F15.wireOp",EDGE,"E39.MirrorCS")]}),-1.0]])],"derivedFrom":subQ1})])]})])],"derivedFrom":makeQuery(id+"F16.opExtrude","CAP_EDGE",EDGE,{"disambiguationData":[OSD([subQ0])],"isStart":true})});}
            var Q1;
            {var subQ0=sQuery(id+"F15.wireOp",EDGE,"E33.0");var subQ1=sQuery(id+"F15.wireOp",EDGE,"E34");Q1=makeQuery(id+"F17.boolean.opBoolean","SPLIT",EDGE,{"disambiguationData":[TD([makeQuery(id+"F17.opExtrude","SWEPT_FACE",FACE,{"disambiguationData":[OSD([subQ1]),TDD([makeQuery(id+"F15.imprint","IMPRINT",EDGE,{"disambiguationData":[TD([[makeQuery(id+"F15.imprint","INTERSECT",VERTEX,{"derivedFrom":[subQ1,sQuery(id+"F15.wireOp",EDGE,"E35")]}),1.0]])],"derivedFrom":subQ1})])]})])],"derivedFrom":makeQuery(id+"F16.opExtrude","CAP_EDGE",EDGE,{"disambiguationData":[OSD([subQ0])],"isStart":true})});}
            var Q2;
            {var subQ0=sQuery(id+"F15.wireOp",EDGE,"E33.0");var subQ1=sQuery(id+"F15.wireOp",EDGE,"E38.MirrorCS");Q2=makeQuery(id+"F17.boolean.opBoolean","SPLIT",EDGE,{"disambiguationData":[TD([makeQuery(id+"F17.opExtrude","SWEPT_FACE",FACE,{"disambiguationData":[OSD([subQ1]),TDD([makeQuery(id+"F15.imprint","IMPRINT",EDGE,{"disambiguationData":[TD([[makeQuery(id+"F15.imprint","INTERSECT",VERTEX,{"derivedFrom":[subQ1,sQuery(id+"F15.wireOp",EDGE,"E40.MirrorCS")]}),1.0]])],"derivedFrom":subQ1})])]})])],"derivedFrom":makeQuery(id+"F16.opExtrude","CAP_EDGE",EDGE,{"disambiguationData":[OSD([subQ0])],"isStart":true})});}
            var Q3;
            {var subQ0=sQuery(id+"F15.wireOp",EDGE,"E33.0");var subQ2=sQuery(id+"F15.wireOp",EDGE,"E34");Q3=makeQuery(id+"F17.boolean.opBoolean","SPLIT",EDGE,{"disambiguationData":[TD([makeQuery(id+"F17.opExtrude","SWEPT_FACE",FACE,{"disambiguationData":[OSD([subQ2]),TDD([makeQuery(id+"F15.imprint","IMPRINT",EDGE,{"disambiguationData":[TD([[makeQuery(id+"F15.imprint","INTERSECT",VERTEX,{"derivedFrom":[subQ2,sQuery(id+"F15.wireOp",EDGE,"E37")]}),-1.0]])],"derivedFrom":subQ2})])]})])],"derivedFrom":makeQuery(id+"F16.opExtrude","CAP_EDGE",EDGE,{"disambiguationData":[OSD([subQ0])],"isStart":true})});}
            var Q4;
            {var subQ0=sQuery(id+"F15.wireOp",EDGE,"E38.MirrorCS");var subQ1=sQuery(id+"F15.wireOp",EDGE,"E32");var subQ2=sQuery(id+"F15.wireOp",EDGE,"E50.0");Q4=makeQuery(id+"F17.boolean.opBoolean","SPLIT",EDGE,{"disambiguationData":[TD([makeQuery(id+"F17.opExtrude","SWEPT_FACE",FACE,{"disambiguationData":[OSD([subQ0]),TDD([makeQuery(id+"F15.imprint","IMPRINT",EDGE,{"disambiguationData":[TD([[makeQuery(id+"F15.imprint","INTERSECT",VERTEX,{"disambiguationData":[OD(1.0)],"derivedFrom":[subQ1,subQ0]}),1.0]])],"derivedFrom":subQ0})])]})])],"derivedFrom":makeQuery(id+"F16.opExtrude","CAP_EDGE",EDGE,{"disambiguationData":[OSD([subQ2])],"isStart":true})});}
            var Q5;
            {var subQ1=sQuery(id+"F15.wireOp",EDGE,"E32");var subQ2=sQuery(id+"F15.wireOp",EDGE,"E50.0");var subQ3=sQuery(id+"F15.wireOp",EDGE,"E38.MirrorCS");Q5=makeQuery(id+"F17.boolean.opBoolean","SPLIT",EDGE,{"disambiguationData":[TD([makeQuery(id+"F17.opExtrude","SWEPT_FACE",FACE,{"disambiguationData":[OSD([subQ3]),TDD([makeQuery(id+"F15.imprint","IMPRINT",EDGE,{"disambiguationData":[TD([[makeQuery(id+"F15.imprint","INTERSECT",VERTEX,{"disambiguationData":[OD(0.0)],"derivedFrom":[subQ1,subQ3]}),-1.0]])],"derivedFrom":subQ3})])]})])],"derivedFrom":makeQuery(id+"F16.opExtrude","CAP_EDGE",EDGE,{"disambiguationData":[OSD([subQ2])],"isStart":true})});}
            var Q6;
            {var subQ0=sQuery(id+"F15.wireOp",EDGE,"E50.0");var subQ1=sQuery(id+"F15.wireOp",EDGE,"E34");var subQ2=sQuery(id+"F15.wireOp",EDGE,"E32");Q6=makeQuery(id+"F17.boolean.opBoolean","SPLIT",EDGE,{"disambiguationData":[TD([makeQuery(id+"F17.opExtrude","SWEPT_FACE",FACE,{"disambiguationData":[OSD([subQ1]),TDD([makeQuery(id+"F15.imprint","IMPRINT",EDGE,{"disambiguationData":[TD([[makeQuery(id+"F15.imprint","INTERSECT",VERTEX,{"disambiguationData":[OD(0.0)],"derivedFrom":[subQ2,subQ1]}),1.0]])],"derivedFrom":subQ1})])]})])],"derivedFrom":makeQuery(id+"F16.opExtrude","CAP_EDGE",EDGE,{"disambiguationData":[OSD([subQ0])],"isStart":true})});}
            var Q7;
            {var subQ0=sQuery(id+"F15.wireOp",EDGE,"E50.0");var subQ2=sQuery(id+"F15.wireOp",EDGE,"E32");var subQ3=sQuery(id+"F15.wireOp",EDGE,"E34");Q7=makeQuery(id+"F17.boolean.opBoolean","SPLIT",EDGE,{"disambiguationData":[TD([makeQuery(id+"F17.opExtrude","SWEPT_FACE",FACE,{"disambiguationData":[OSD([subQ3]),TDD([makeQuery(id+"F15.imprint","IMPRINT",EDGE,{"disambiguationData":[TD([[makeQuery(id+"F15.imprint","INTERSECT",VERTEX,{"disambiguationData":[OD(1.0)],"derivedFrom":[subQ2,subQ3]}),-1.0]])],"derivedFrom":subQ3})])]})])],"derivedFrom":makeQuery(id+"F16.opExtrude","CAP_EDGE",EDGE,{"disambiguationData":[OSD([subQ0])],"isStart":true})});}
            var Q8;
            Q8=makeQuery(id+"F8.opRevolve","SWEPT_EDGE",EDGE,{"disambiguationData":[OSD([sQuery(id+"F0.wireOp",EDGE,"E0"),sQuery(id+"F0.wireOp",EDGE,"E1")])]});
            var Q9;
            {var subQ1=sQuery(id+"F15.wireOp",EDGE,"E32");var subQ3=sQuery(id+"F15.wireOp",EDGE,"E38.MirrorCS");Q9=makeQuery(id+"F17.boolean.opBoolean","SPLIT",EDGE,{"disambiguationData":[TD([makeQuery(id+"F17.opExtrude","SWEPT_FACE",FACE,{"disambiguationData":[OSD([subQ3]),TDD([makeQuery(id+"F15.imprint","IMPRINT",EDGE,{"disambiguationData":[TD([[makeQuery(id+"F15.imprint","INTERSECT",VERTEX,{"disambiguationData":[OD(0.0)],"derivedFrom":[subQ1,subQ3]}),-1.0]])],"derivedFrom":subQ3})])]})])],"derivedFrom":makeQuery(id+"F16.opExtrude","CAP_EDGE",EDGE,{"disambiguationData":[OSD([subQ1])],"isStart":true})});}
            var Q10;
            {var subQ0=sQuery(id+"F15.wireOp",EDGE,"E32");var subQ1=sQuery(id+"F15.wireOp",EDGE,"E34");Q10=makeQuery(id+"F17.boolean.opBoolean","SPLIT",EDGE,{"disambiguationData":[TD([makeQuery(id+"F17.opExtrude","SWEPT_FACE",FACE,{"disambiguationData":[OSD([subQ1]),TDD([makeQuery(id+"F15.imprint","IMPRINT",EDGE,{"disambiguationData":[TD([[makeQuery(id+"F15.imprint","INTERSECT",VERTEX,{"disambiguationData":[OD(1.0)],"derivedFrom":[subQ0,subQ1]}),-1.0]])],"derivedFrom":subQ1})])]})])],"derivedFrom":makeQuery(id+"F16.opExtrude","CAP_EDGE",EDGE,{"disambiguationData":[OSD([subQ0])],"isStart":true})});}
            var Q11;
            {var subQ0=sQuery(id+"F15.wireOp",EDGE,"E32");var subQ1=sQuery(id+"F15.wireOp",EDGE,"E34");Q11=makeQuery(id+"F17.boolean.opBoolean","SPLIT",EDGE,{"disambiguationData":[TD([makeQuery(id+"F17.opExtrude","SWEPT_FACE",FACE,{"disambiguationData":[OSD([subQ1]),TDD([makeQuery(id+"F15.imprint","IMPRINT",EDGE,{"disambiguationData":[TD([[makeQuery(id+"F15.imprint","INTERSECT",VERTEX,{"disambiguationData":[OD(0.0)],"derivedFrom":[subQ0,subQ1]}),1.0]])],"derivedFrom":subQ1})])]})])],"derivedFrom":makeQuery(id+"F16.opExtrude","CAP_EDGE",EDGE,{"disambiguationData":[OSD([subQ0])],"isStart":true})});}
            var Q12;
            {var subQ0=sQuery(id+"F15.wireOp",EDGE,"E38.MirrorCS");var subQ1=sQuery(id+"F15.wireOp",EDGE,"E32");Q12=makeQuery(id+"F17.boolean.opBoolean","SPLIT",EDGE,{"disambiguationData":[TD([makeQuery(id+"F17.opExtrude","SWEPT_FACE",FACE,{"disambiguationData":[OSD([subQ0]),TDD([makeQuery(id+"F15.imprint","IMPRINT",EDGE,{"disambiguationData":[TD([[makeQuery(id+"F15.imprint","INTERSECT",VERTEX,{"disambiguationData":[OD(1.0)],"derivedFrom":[subQ1,subQ0]}),1.0]])],"derivedFrom":subQ0})])]})])],"derivedFrom":makeQuery(id+"F16.opExtrude","CAP_EDGE",EDGE,{"disambiguationData":[OSD([subQ1])],"isStart":true})});}
            fillet(context, id + "F18", {"entities" : qUnion([Q0, Q1, Q2, Q3, Q4, Q5, Q6, Q7, Q8, Q9, Q10, Q11, Q12]), "radius" : 0.5 * mm, "tangentPropagation" : true, "allowEdgeOverflow" : false});
        }
        {
            var Q0;
            Q0=makeQuery(id+"F17.opExtrude","CAP_EDGE",EDGE,{"disambiguationData":[OSD([sQuery(id+"F15.wireOp",EDGE,"E48.MirrorCS"),sQuery(id+"F15.wireOp",EDGE,"E49.MirrorCS")])],"isStart":false});
            var Q1;
            Q1=makeQuery(id+"F17.opExtrude","CAP_EDGE",EDGE,{"disambiguationData":[OSD([sQuery(id+"F15.wireOp",EDGE,"E35"),sQuery(id+"F15.wireOp",EDGE,"E40.MirrorCS")])],"isStart":false});
            var Q2;
            Q2=makeQuery(id+"F17.opExtrude","CAP_EDGE",EDGE,{"disambiguationData":[OSD([sQuery(id+"F15.wireOp",EDGE,"E42"),sQuery(id+"F15.wireOp",EDGE,"E44.MirrorCS")])],"isStart":false});
            var Q3;
            Q3=makeQuery(id+"F17.opExtrude","CAP_EDGE",EDGE,{"disambiguationData":[OSD([sQuery(id+"F15.wireOp",EDGE,"E37"),sQuery(id+"F15.wireOp",EDGE,"E39.MirrorCS")])],"isStart":false});
            fillet(context, id + "F19", {"entities" : qUnion([Q0, Q1, Q2, Q3]), "radius" : 5 * mm, "tangentPropagation" : true, "allowEdgeOverflow" : false});
        }
    });
